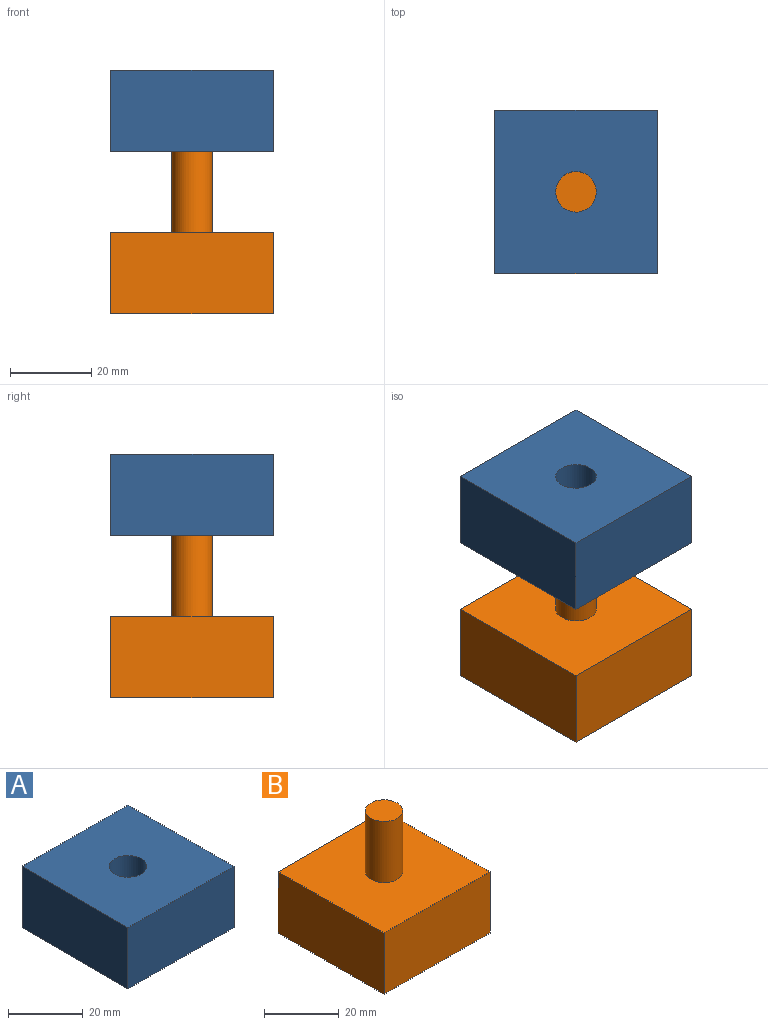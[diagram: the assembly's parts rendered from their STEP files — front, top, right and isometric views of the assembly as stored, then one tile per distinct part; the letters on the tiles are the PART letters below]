
ASSEMBLY  parts=2 mates=1
PART A: 7 faces, bbox 40x40x20 mm
  f0: plane 40x20mm, normal (0,-1,0), area 800mm2, adj f1,f3,f4,f5
  f1: plane 40x20mm, normal (1,0,0), area 800mm2, adj f0,f2,f4,f5
  f2: plane 40x20mm, normal (0,1,0), area 800mm2, adj f1,f3,f4,f5
  f3: plane 40x20mm, normal (-1,0,0), area 800mm2, adj f0,f2,f4,f5
  f4: plane 40x40mm, normal (0,0,1), area 1521.5mm2, adj f0,f1,f2,f3,f6
  f5: plane 40x40mm, normal (0,0,-1), area 1521.5mm2, adj f0,f1,f2,f3,f6
  f6: cylinder r=5mm len=20mm, axis (0,0,1), area 628.3mm2, adj f4,f5
PART B: 8 faces, bbox 40x40x40 mm
  f0: plane 40x20mm, normal (0,-1,0), area 800mm2, adj f1,f3,f4,f5
  f1: plane 40x20mm, normal (1,0,0), area 800mm2, adj f0,f2,f4,f5
  f2: plane 40x20mm, normal (0,1,0), area 800mm2, adj f1,f3,f4,f5
  f3: plane 40x20mm, normal (-1,0,0), area 800mm2, adj f0,f2,f4,f5
  f4: plane 40x40mm, normal (0,0,1), area 1521.5mm2, adj f0,f1,f2,f3,f6
  f5: plane 40x40mm, normal (0,0,-1), area 1600mm2, adj f0,f1,f2,f3
  f6: cylinder r=5mm len=20mm, axis (0,0,-1), area 628.3mm2, adj f4,f7
  f7: plane 10x10mm, normal (0,0,1), area 78.5mm2, adj f6
PLACE A at identity fixed
PLACE B t=(0,-64,-40)mm
MATE slider A.f6 <-> B.f6  axis (0,0,1) through (0,0,20)mm
